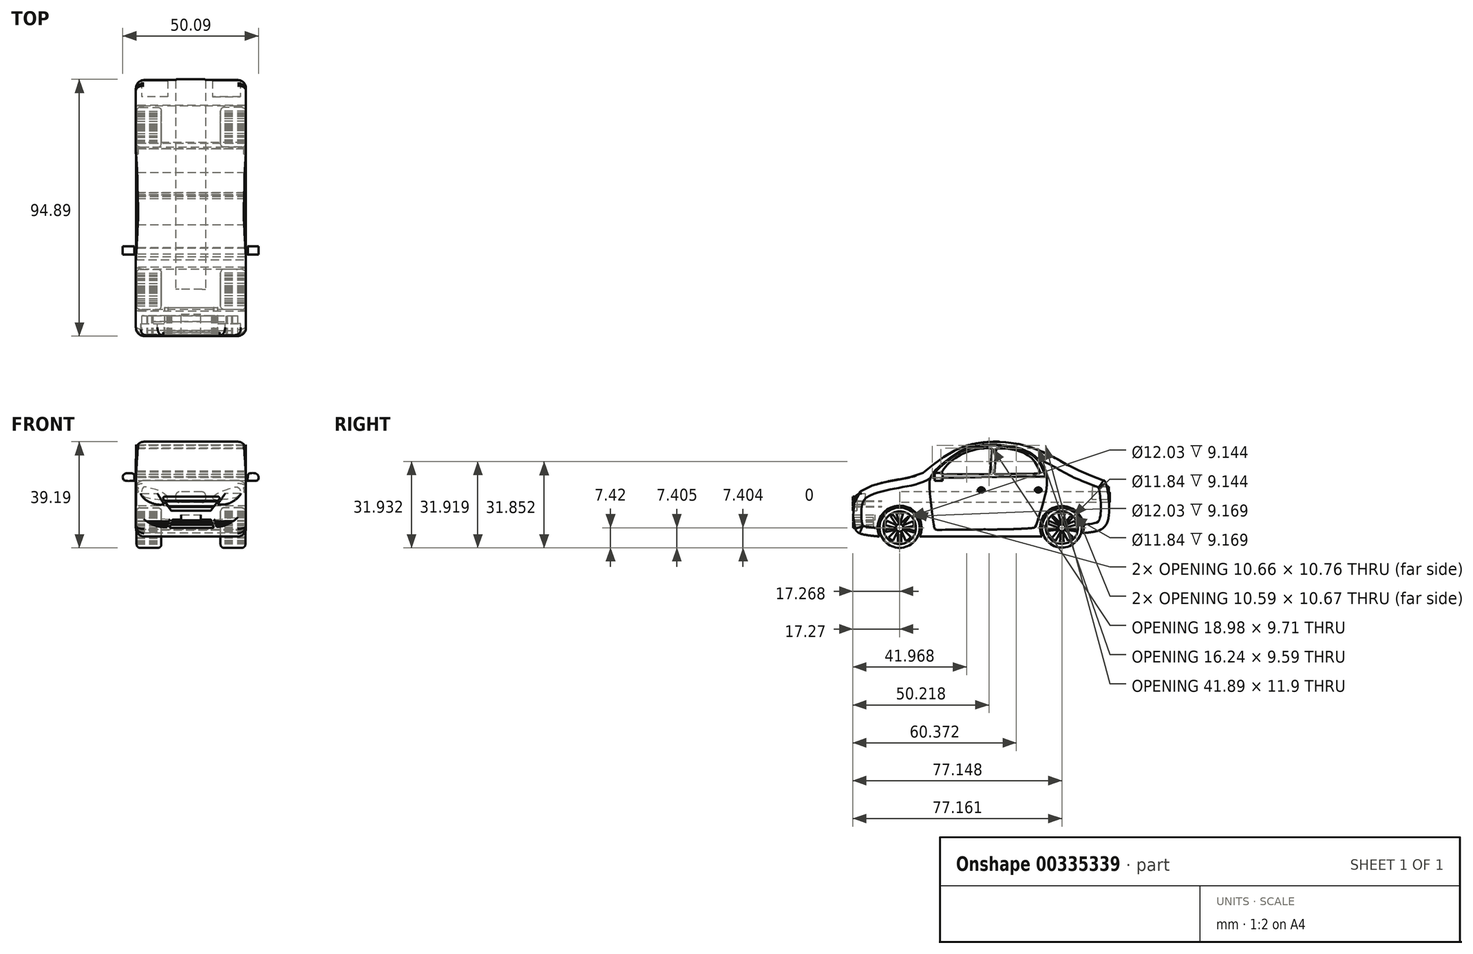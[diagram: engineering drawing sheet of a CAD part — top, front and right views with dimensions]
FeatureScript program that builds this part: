
annotation { "Feature Type Name" : "Feature", "Feature Type Description" : "" }
export const myFeature = defineFeature(function(context is Context, id is Id, definition is map)
    precondition{}
    {
        {
            var Q0;
            Q0=qCreatedBy(makeId("Right.planeOp"),FACE);
            var sketch = newSketch(context, id + "F0", { "sketchPlane" : qUnion([Q0])});
            skCircle(sketch, "E0", {"center": v(0, 0) * mm, "radius": 7.42 * mm});
            skFitSpline(sketch, "E1", {"points": [v(-7.45, -3.27) * mm, v(-16.56, 0) * mm, v(-16.39, 10.61) * mm, v(-12.18, 14.74) * mm, v(-4.1, 17.13) * mm, v(3.13, 18.48) * mm, v(8.44, 20.18) * mm, v(12.58, 23.47) * mm, v(21.8, 29.37) * mm, v(24.6, 30.4) * mm, v(33.03, 31.7) * mm, v(44.35, 30.84) * mm, v(52.91, 27.94) * mm, v(59.85, 24.44) * mm, v(65.24, 21.51) * mm, v(75.37, 17.46) * mm, v(75.38, 17.47) * mm, v(75.88, 16.98) * mm, v(76.75, 2.34) * mm, v(71.8, -1.45) * mm, v(67.68, -1.97) * mm], "startDerivative": vector(-334.75, 36.18) * mm, "endDerivative": vector(-1.84, -0.27) * mm});
            skCircle(sketch, "E2", {"center": v(59.9, -0.02) * mm, "radius": 7.32 * mm});
            skArc(sketch, "E3", {"start": v(7.45, -3.27) * mm, "mid": v(0, 8.13) * mm, "end": v(-7.45, -3.27) * mm});
            skLineSegment(sketch, "E4", {"start": v(7.45, -3.27) * mm, "end": v(52.55, -3.27) * mm});
            skArc(sketch, "E5", {"start": v(67.68, -1.97) * mm, "mid": v(59.2, 7.99) * mm, "end": v(52.55, -3.27) * mm});
            skLineSegment(sketch, "E6", {"start": v(12, 18.48) * mm, "end": v(23.8, 18.48) * mm});
            skLineSegment(sketch, "E7", {"start": v(23.8, 18.48) * mm, "end": v(43.08, 18.82) * mm});
            skFitSpline(sketch, "E8", {"points": [v(43.08, 18.82) * mm, v(53.9, 18.82) * mm], "startDerivative": vector(13.95, 0.43) * mm, "endDerivative": vector(1.45, 0) * mm});
            skFitSpline(sketch, "E9", {"points": [v(12, 18.48) * mm, v(15.51, 22.85) * mm, v(19.98, 26.4) * mm, v(24.84, 28.92) * mm, v(33.06, 30.36) * mm, v(40.04, 29.97) * mm, v(45.26, 28.72) * mm, v(50.5, 25.42) * mm, v(53.9, 18.82) * mm], "startDerivative": vector(25.41, 56.18) * mm, "endDerivative": vector(25.34, -69.35) * mm});
            skLineSegment(sketch, "E10", {"start": v(34.19, 29.32) * mm, "end": v(33.38, 20.5) * mm});
            skLineSegment(sketch, "E11", {"start": v(35.73, 29.3) * mm, "end": v(34.98, 20.88) * mm});
            skFitSpline(sketch, "E12", {"points": [v(33.38, 20.5) * mm, v(33.2, 20.01) * mm, v(32.93, 19.76) * mm, v(32.45, 19.72) * mm, v(30.27, 19.76) * mm, v(15.2, 19.64) * mm], "startDerivative": vector(-1.6, -4.7) * mm, "endDerivative": vector(-36.28, -1.14) * mm});
            skFitSpline(sketch, "E13", {"points": [v(15.2, 19.64) * mm, v(16.6, 22.1) * mm, v(18.32, 23.94) * mm, v(20.98, 26.05) * mm, v(25.02, 27.98) * mm, v(27.97, 28.86) * mm, v(30.54, 29.28) * mm, v(32.47, 29.35) * mm, v(34.19, 29.32) * mm], "startDerivative": vector(6.96, 20.98) * mm, "endDerivative": vector(24.38, -0.14) * mm});
            skFitSpline(sketch, "E14", {"points": [v(34.98, 20.88) * mm, v(35.04, 19.85) * mm, v(35.75, 19.7) * mm, v(43.29, 19.88) * mm, v(51.97, 20.16) * mm, v(51.95, 20.3) * mm, v(50.47, 23.41) * mm, v(47.13, 26.96) * mm, v(43.21, 28.54) * mm, v(39.6, 29.2) * mm, v(35.78, 29.33) * mm, v(35.73, 29.3) * mm], "startDerivative": vector(-4.72, -21.76) * mm, "endDerivative": vector(1.65, -5.9) * mm});
            skFitSpline(sketch, "E15", {"points": [v(34.5, -0.66) * mm, v(31.8, -0.62) * mm, v(27.92, -0.7) * mm, v(15.04, -0.78) * mm, v(13.15, -0.6) * mm, v(12.51, 1.6) * mm, v(11.04, 14.54) * mm, v(11.29, 18.17) * mm, v(12.52, 20.44) * mm, v(13.88, 21.92) * mm, v(16.21, 24.02) * mm, v(17.77, 25.17) * mm, v(19.2, 26.3) * mm, v(21.87, 27.98) * mm, v(23.84, 29.05) * mm, v(26.88, 29.97) * mm, v(30.6, 30.49) * mm, v(33.38, 30.65) * mm, v(35.1, 30.65) * mm, v(38.49, 30.38) * mm, v(42.51, 29.8) * mm, v(44.35, 29.3) * mm, v(46.82, 28.37) * mm, v(49.37, 26.86) * mm, v(51.44, 24.92) * mm, v(53.07, 22.03) * mm, v(53.74, 20.2) * mm, v(54.2, 18.85) * mm, v(54.33, 17.3) * mm, v(54.18, 14.27) * mm, v(52.5, 7.62) * mm, v(50.23, 0.57) * mm, v(49.5, 0) * mm, v(38.73, -0.6) * mm, v(35.9, -0.63) * mm], "startDerivative": vector(-90.1, -4.33) * mm, "endDerivative": vector(-24.37, -0.8) * mm});
            skFitSpline(sketch, "E16", {"points": [v(34.5, -0.66) * mm, v(35.9, -0.63) * mm], "startDerivative": vector(0.82, 0.03) * mm, "endDerivative": vector(0.82, 0.03) * mm});
            skPoint(sketch, "E17.6.internal.snap0", {"position": v(33.78, 24.9) * mm});
            skFitSpline(sketch, "E17", {"points": [v(34.5, -0.66) * mm, v(33.58, 3.26) * mm, v(33.05, 7.57) * mm, v(32.77, 11.15) * mm, v(32.78, 13.96) * mm, v(33.21, 16.71) * mm, v(33.55, 19) * mm, v(34.08, 20.94) * mm, v(34.48, 24.55) * mm, v(34.98, 28.83) * mm, v(35.29, 30.64) * mm], "startDerivative": vector(-4.87, 22.56) * mm, "endDerivative": vector(2.72, 18.18) * mm});
            skFitSpline(sketch, "E18", {"points": [v(9.31, 20.82) * mm, v(10.43, 21.67) * mm, v(11.82, 22.88) * mm, v(13, 23.95) * mm, v(14.9, 25.3) * mm, v(16.2, 26.21) * mm, v(17.35, 26.94) * mm, v(18.48, 27.6) * mm, v(20.2, 28.7) * mm, v(21.78, 29.54) * mm, v(22.77, 29.98) * mm, v(23.55, 30.22) * mm], "startDerivative": vector(16.6, 10.33) * mm, "endDerivative": vector(11.57, 3.51) * mm});
            skArc(sketch, "E19", {"start": v(31.46, 13.96) * mm, "mid": v(30.14, 14.92) * mm, "end": v(28.81, 13.96) * mm});
            skArc(sketch, "E20", {"start": v(28.81, 13.96) * mm, "mid": v(30.14, 13) * mm, "end": v(31.46, 13.96) * mm});
            skLineSegment(sketch, "E21", {"start": v(28.94, 14.24) * mm, "end": v(31.46, 14.28) * mm});
            skLineSegment(sketch, "E22", {"start": v(28.9, 13.74) * mm, "end": v(31.37, 13.74) * mm});
            skLineSegment(sketch, "E23", {"start": v(49.96, 14.17) * mm, "end": v(52.4, 14.17) * mm});
            skLineSegment(sketch, "E24", {"start": v(50, 13.65) * mm, "end": v(52.35, 13.65) * mm});
            skArc(sketch, "E25", {"start": v(52.49, 13.96) * mm, "mid": v(51.18, 14.9) * mm, "end": v(49.87, 13.96) * mm});
            skArc(sketch, "E26", {"start": v(49.87, 13.96) * mm, "mid": v(51.18, 12.98) * mm, "end": v(52.49, 13.96) * mm});
            skCircle(sketch, "E27", {"center": v(0, 0) * mm, "radius": 6.02 * mm});
            skCircle(sketch, "E28", {"center": v(0, 0) * mm, "radius": 5.38 * mm});
            skCircle(sketch, "E29", {"center": v(0, 0) * mm, "radius": 1.37 * mm});
            skLineSegment(sketch, "E30", {"start": v(-1.2, 5.24) * mm, "end": v(-0.05, 1.36) * mm});
            skLineSegment(sketch, "E31", {"start": v(-0.05, 1.36) * mm, "end": v(-2.4, 4.82) * mm});
            skLineSegment(sketch, "E32", {"start": v(0.13, 1.36) * mm, "end": v(1.3, 5.22) * mm});
            skLineSegment(sketch, "E33", {"start": v(0.13, 1.36) * mm, "end": v(3.31, 4.24) * mm});
            skLineSegment(sketch, "E34", {"start": v(-1.06, 0.86) * mm, "end": v(-3.34, 4.22) * mm});
            skLineSegment(sketch, "E35", {"start": v(-1.06, 0.86) * mm, "end": v(-4.72, 2.58) * mm});
            skLineSegment(sketch, "E36", {"start": v(3.6, 4) * mm, "end": v(1.1, 0.81) * mm});
            skLineSegment(sketch, "E37", {"start": v(1.1, 0.81) * mm, "end": v(4.86, 2.3) * mm});
            skLineSegment(sketch, "E38", {"start": v(-1.37, 0) * mm, "end": v(-5.3, 0.97) * mm});
            skLineSegment(sketch, "E39", {"start": v(-1.37, 0) * mm, "end": v(-5.33, -0.7) * mm});
            skLineSegment(sketch, "E40", {"start": v(-1.18, -0.69) * mm, "end": v(-5.15, -1.54) * mm});
            skLineSegment(sketch, "E41", {"start": v(-1.18, -0.69) * mm, "end": v(-4.01, -3.58) * mm});
            skLineSegment(sketch, "E42", {"start": v(1.37, 0) * mm, "end": v(5.33, 0.72) * mm});
            skLineSegment(sketch, "E43", {"start": v(1.37, 0) * mm, "end": v(5.26, -1.1) * mm});
            skLineSegment(sketch, "E44", {"start": v(1.22, -0.61) * mm, "end": v(5.12, -1.65) * mm});
            skLineSegment(sketch, "E45", {"start": v(1.22, -0.61) * mm, "end": v(4.13, -3.45) * mm});
            skLineSegment(sketch, "E46", {"start": v(-2.4, -4.82) * mm, "end": v(-0.6, -1.23) * mm});
            skLineSegment(sketch, "E47", {"start": v(-0.6, -1.23) * mm, "end": v(-0.7, -5.33) * mm});
            skLineSegment(sketch, "E48", {"start": v(0.57, -5.35) * mm, "end": v(0.57, -1.24) * mm});
            skLineSegment(sketch, "E49", {"start": v(0.57, -1.24) * mm, "end": v(2.25, -4.88) * mm});
            skCircle(sketch, "E50", {"center": v(59.9, -0.02) * mm, "radius": 5.92 * mm});
            skCircle(sketch, "E51", {"center": v(59.9, -0.02) * mm, "radius": 5.33 * mm});
            skCircle(sketch, "E52", {"center": v(59.9, -0.02) * mm, "radius": 1.26 * mm});
            skLineSegment(sketch, "E53", {"start": v(60.27, 1.19) * mm, "end": v(60.93, 5.22) * mm});
            skLineSegment(sketch, "E54", {"start": v(60.27, 1.19) * mm, "end": v(63.08, 4.26) * mm});
            skLineSegment(sketch, "E55", {"start": v(58.63, 5.17) * mm, "end": v(59.77, 1.24) * mm});
            skLineSegment(sketch, "E56", {"start": v(59.77, 1.24) * mm, "end": v(56.79, 4.32) * mm});
            skLineSegment(sketch, "E57", {"start": v(56.27, 3.9) * mm, "end": v(59, 0.88) * mm});
            skLineSegment(sketch, "E58", {"start": v(59, 0.88) * mm, "end": v(55.18, 2.48) * mm});
            skLineSegment(sketch, "E59", {"start": v(60.8, 0.87) * mm, "end": v(63.77, 3.65) * mm});
            skLineSegment(sketch, "E60", {"start": v(60.8, 0.87) * mm, "end": v(64.6, 2.47) * mm});
            skLineSegment(sketch, "E61", {"start": v(60.6, -5.3) * mm, "end": v(60.17, -1.25) * mm});
            skPoint(sketch, "E61.startSnap0", {"position": v(60.6, 3.2) * mm});
            skLineSegment(sketch, "E62", {"start": v(60.17, -1.25) * mm, "end": v(62.16, -4.84) * mm});
            skLineSegment(sketch, "E63", {"start": v(59.15, -5.3) * mm, "end": v(59.59, -1.24) * mm});
            skLineSegment(sketch, "E64", {"start": v(59.59, -1.24) * mm, "end": v(57.58, -4.82) * mm});
            skLineSegment(sketch, "E65", {"start": v(61.15, 0.1) * mm, "end": v(65.1, 1.12) * mm});
            skLineSegment(sketch, "E66", {"start": v(61.15, 0.1) * mm, "end": v(65.18, -0.73) * mm});
            skLineSegment(sketch, "E67", {"start": v(65.05, -1.38) * mm, "end": v(60.97, -0.67) * mm});
            skLineSegment(sketch, "E68", {"start": v(60.97, -0.67) * mm, "end": v(64, -3.43) * mm});
            skLineSegment(sketch, "E69", {"start": v(58.63, 0) * mm, "end": v(54.77, 1.47) * mm});
            skLineSegment(sketch, "E70", {"start": v(58.63, 0) * mm, "end": v(54.58, -0.51) * mm});
            skLineSegment(sketch, "E71", {"start": v(54.69, -1.18) * mm, "end": v(58.84, -0.72) * mm});
            skLineSegment(sketch, "E72", {"start": v(58.84, -0.72) * mm, "end": v(56.16, -3.82) * mm});
            skFitSpline(sketch, "E73", {"points": [v(67.76, -1.96) * mm, v(67.68, -1.97) * mm], "startDerivative": vector(-0.1, 0) * mm, "endDerivative": vector(-0.05, 0) * mm});
            skFitSpline(sketch, "E74", {"points": [v(63.64, 22.4) * mm, v(59.31, 24.8) * mm, v(56.3, 26.43) * mm, v(54.3, 27.37) * mm, v(50.96, 28.83) * mm, v(49.58, 29.37) * mm, v(48.2, 29.85) * mm], "startDerivative": vector(-23.68, 12.38) * mm, "endDerivative": vector(-10.9, 3.6) * mm});
            skFitSpline(sketch, "E75", {"points": [v(67.77, -1.99) * mm, v(68.13, -1.96) * mm, v(68.42, -1.93) * mm, v(69.26, -1.86) * mm, v(70.44, -1.71) * mm, v(70.82, -1.66) * mm, v(71.21, -1.6) * mm, v(71.94, -1.48) * mm, v(73.05, -1.24) * mm, v(73.32, -1.18) * mm, v(73.58, -1.08) * mm, v(73.78, -1) * mm, v(73.96, -0.9) * mm, v(74.23, -0.8) * mm, v(74.42, -0.7) * mm, v(74.66, -0.57) * mm, v(74.78, -0.48) * mm, v(74.94, -0.39) * mm, v(75.25, -0.11) * mm, v(75.42, 0.03) * mm, v(75.56, 0.15) * mm, v(75.69, 0.29) * mm, v(75.82, 0.44) * mm, v(75.92, 0.6) * mm, v(75.96, 0.64) * mm, v(76, 0.7) * mm, v(76.01, 0.73) * mm, v(76.07, 0.82) * mm, v(76.14, 0.92) * mm, v(76.23, 1.07) * mm, v(76.33, 1.26) * mm, v(76.46, 1.51) * mm, v(76.47, 1.55) * mm, v(76.49, 1.6) * mm, v(76.5, 1.65) * mm], "startDerivative": vector(11.27, 0.92) * mm, "endDerivative": vector(3.7, 8.89) * mm});
            skSolve(sketch);
        }
        {
            var Q0;
            Q0=makeQuery(id+"F0.imprint","IMPRINT",FACE,{"disambiguationData":[TD([[makeQuery(id+"F0.imprint","IMPRINT",EDGE,{"derivedFrom":sQuery(id+"F0.wireOp",EDGE,"E1")}),-1.0]])]});
            extrude(context, id + "F1", {"entities" : qUnion([Q0]), "depth" : 20.32 * mm, "hasSecondDirection" : true, "secondDirectionOppositeDirection" : true, "secondDirectionDepth" : 20.32 * mm});
        }
        {
            var Q0;
            Q0=makeQuery(id+"F0.imprint","IMPRINT",FACE,{"disambiguationData":[TD([[makeQuery(id+"F0.imprint","IMPRINT",EDGE,{"derivedFrom":sQuery(id+"F0.wireOp",EDGE,"E10")}),-1.0]])]});
            var Q1;
            Q1=makeQuery(id+"F0.imprint","IMPRINT",FACE,{"disambiguationData":[TD([[makeQuery(id+"F0.imprint","IMPRINT",EDGE,{"derivedFrom":sQuery(id+"F0.wireOp",EDGE,"E11")}),1.0]])]});
            extrude(context, id + "F2", {"entities" : qUnion([Q0, Q1]), "depth" : 20.07 * mm, "hasSecondDirection" : true, "secondDirectionOppositeDirection" : true, "secondDirectionDepth" : 20.07 * mm});
        }
        {
            var Q0;
            {var subQ1=sQuery(id+"F0.wireOp",EDGE,"E6");Q0=makeQuery(id+"F0.imprint","IMPRINT",FACE,{"disambiguationData":[TD([[makeQuery(id+"F0.imprint","IMPRINT",EDGE,{"derivedFrom":subQ1}),1.0]])]});}
            var Q1;
            {var subQ1=sQuery(id+"F0.wireOp",EDGE,"E8");Q1=makeQuery(id+"F0.imprint","IMPRINT",FACE,{"disambiguationData":[TD([[makeQuery(id+"F0.imprint","IMPRINT",EDGE,{"derivedFrom":subQ1}),1.0]])]});}
            extrude(context, id + "F3", {"entities" : qUnion([Q0, Q1]), "depth" : 20.14 * mm, "hasSecondDirection" : true, "secondDirectionOppositeDirection" : true, "secondDirectionDepth" : 20.14 * mm});
        }
        {
            var Q0;
            {var subQ1=sQuery(id+"F0.wireOp",EDGE,"E8");Q0=makeQuery(id+"F0.imprint","IMPRINT",FACE,{"disambiguationData":[TD([[makeQuery(id+"F0.imprint","IMPRINT",EDGE,{"derivedFrom":subQ1}),-1.0]])]});}
            var Q1;
            {var subQ1=sQuery(id+"F0.wireOp",EDGE,"E6");Q1=makeQuery(id+"F0.imprint","IMPRINT",FACE,{"disambiguationData":[TD([[makeQuery(id+"F0.imprint","IMPRINT",EDGE,{"derivedFrom":subQ1}),-1.0]])]});}
            extrude(context, id + "F4", {"entities" : qUnion([Q0, Q1]), "depth" : 20.24 * mm, "hasSecondDirection" : true, "secondDirectionOppositeDirection" : true, "secondDirectionDepth" : 20.24 * mm});
        }
        {
            var Q0;
            Q0=sQuery(id+"F0.wireOp",EDGE,"E17");
            extrude(context, id + "F5", {"bodyType" : ToolBodyType.SURFACE, "surfaceEntities" : qUnion([Q0]), "depth" : 20.17 * mm, "hasSecondDirection" : true, "secondDirectionOppositeDirection" : true, "secondDirectionDepth" : 20.17 * mm});
        }
        {
            var Q0;
            Q0=qCreatedBy(makeId("Front.planeOp"),FACE);
            var sketch = newSketch(context, id + "F6", { "sketchPlane" : qUnion([Q0])});
            skLineSegment(sketch, "E76", {"start": v(18.39, 12.66) * mm, "end": v(12.65, 12.66) * mm});
            skLineSegment(sketch, "E77", {"start": v(12.65, 12.66) * mm, "end": v(9.9, 8.59) * mm});
            skFitSpline(sketch, "E78", {"points": [v(9.9, 8.59) * mm, v(13.32, 8.77) * mm, v(15.04, 9.46) * mm, v(16.44, 10.37) * mm, v(18.39, 12.66) * mm], "startDerivative": vector(11.8, -1.45) * mm, "endDerivative": vector(2.65, 9.5) * mm});
            skLineSegment(sketch, "E79", {"start": v(-18.43, 12.66) * mm, "end": v(-12.37, 12.66) * mm});
            skPoint(sketch, "E79.startSnap0", {"position": v(15.52, 12.66) * mm});
            skLineSegment(sketch, "E80", {"start": v(-12.37, 12.66) * mm, "end": v(-9.87, 8.59) * mm});
            skFitSpline(sketch, "E81", {"points": [v(-18.43, 12.66) * mm, v(-17.56, 11.07) * mm, v(-16.28, 10.01) * mm, v(-14.96, 9.33) * mm, v(-13.42, 8.77) * mm, v(-12.15, 8.55) * mm, v(-9.87, 8.59) * mm], "startDerivative": vector(-1.23, -8.9) * mm, "endDerivative": vector(19.02, 1.78) * mm});
            skLineSegment(sketch, "E82", {"start": v(-9.74, 11.45) * mm, "end": v(10.07, 11.45) * mm});
            skLineSegment(sketch, "E83", {"start": v(10.48, 10.64) * mm, "end": v(7.42, 6.46) * mm});
            skLineSegment(sketch, "E84", {"start": v(7, 6.25) * mm, "end": v(-7.04, 6.25) * mm});
            skLineSegment(sketch, "E85", {"start": v(-7.47, 6.49) * mm, "end": v(-10.16, 10.66) * mm});
            skPoint(sketch, "E86.visualSharp", {"position": v(-10.67, 11.45) * mm});
            skArc(sketch, "E86.filletArc", {"start": v(-9.74, 11.45) * mm, "mid": v(-10.18, 11.18) * mm, "end": v(-10.16, 10.66) * mm});
            skPoint(sketch, "E87.visualSharp", {"position": v(11.07, 11.45) * mm});
            skArc(sketch, "E87.filletArc", {"start": v(10.48, 10.64) * mm, "mid": v(10.52, 11.17) * mm, "end": v(10.07, 11.45) * mm});
            skPoint(sketch, "E88.visualSharp", {"position": v(7.27, 6.25) * mm});
            skArc(sketch, "E88.filletArc", {"start": v(7, 6.25) * mm, "mid": v(7.24, 6.3) * mm, "end": v(7.42, 6.46) * mm});
            skPoint(sketch, "E89.visualSharp", {"position": v(-7.32, 6.25) * mm});
            skArc(sketch, "E89.filletArc", {"start": v(-7.47, 6.49) * mm, "mid": v(-7.29, 6.32) * mm, "end": v(-7.04, 6.25) * mm});
            skLineSegment(sketch, "E90", {"start": v(-9.74, 10) * mm, "end": v(10.01, 10) * mm});
            skLineSegment(sketch, "E91", {"start": v(-9.57, 9.74) * mm, "end": v(9.82, 9.74) * mm});
            skLineSegment(sketch, "E92", {"start": v(-8.45, 8) * mm, "end": v(8.55, 8) * mm});
            skLineSegment(sketch, "E93", {"start": v(-8.27, 7.73) * mm, "end": v(8.35, 7.73) * mm});
            skLineSegment(sketch, "E94", {"start": v(-6.7, 3) * mm, "end": v(7.3, 3) * mm});
            skLineSegment(sketch, "E95", {"start": v(7.5, 2.86) * mm, "end": v(8.38, 0.27) * mm});
            skLineSegment(sketch, "E96", {"start": v(8.19, 0) * mm, "end": v(-7.6, 0) * mm});
            skLineSegment(sketch, "E97", {"start": v(-7.8, 0.27) * mm, "end": v(-6.88, 2.86) * mm});
            skLineSegment(sketch, "E98", {"start": v(8.63, 2.68) * mm, "end": v(9.45, 0.26) * mm});
            skLineSegment(sketch, "E99", {"start": v(8.8, 2.95) * mm, "end": v(17.3, 3.88) * mm});
            skArc(sketch, "E100", {"start": v(9.45, 0.26) * mm, "mid": v(13.72, 1.34) * mm, "end": v(17.3, 3.88) * mm});
            skLineSegment(sketch, "E101", {"start": v(-7.84, 2.67) * mm, "end": v(-8.77, 0.21) * mm});
            skLineSegment(sketch, "E102", {"start": v(-8, 2.95) * mm, "end": v(-18.1, 3.88) * mm});
            skArc(sketch, "E103", {"start": v(-18.1, 3.88) * mm, "mid": v(-13.84, 1.03) * mm, "end": v(-8.77, 0.21) * mm});
            skLineSegment(sketch, "E104", {"start": v(-7.08, 2.3) * mm, "end": v(7.69, 2.3) * mm});
            skLineSegment(sketch, "E105", {"start": v(7.69, 2.3) * mm, "end": v(7.76, 2.09) * mm});
            skLineSegment(sketch, "E106", {"start": v(7.76, 2.09) * mm, "end": v(-7.16, 2.09) * mm});
            skLineSegment(sketch, "E107", {"start": v(8.04, 1.26) * mm, "end": v(-7.45, 1.26) * mm});
            skLineSegment(sketch, "E108", {"start": v(-7.45, 1.26) * mm, "end": v(-7.52, 1.04) * mm});
            skLineSegment(sketch, "E109", {"start": v(-7.52, 1.04) * mm, "end": v(8.12, 1.04) * mm});
            skLineSegment(sketch, "E110", {"start": v(-7.97, 2.3) * mm, "end": v(-16.24, 2.3) * mm});
            skLineSegment(sketch, "E111", {"start": v(-8.06, 2.09) * mm, "end": v(-15.91, 2.09) * mm});
            skLineSegment(sketch, "E112", {"start": v(-8.37, 1.26) * mm, "end": v(-14.38, 1.26) * mm});
            skLineSegment(sketch, "E113", {"start": v(-8.46, 1.04) * mm, "end": v(-13.85, 1.04) * mm});
            skLineSegment(sketch, "E114", {"start": v(8.75, 2.3) * mm, "end": v(15.43, 2.3) * mm});
            skLineSegment(sketch, "E115", {"start": v(8.83, 2.09) * mm, "end": v(15.1, 2.09) * mm});
            skLineSegment(sketch, "E116", {"start": v(9.11, 1.26) * mm, "end": v(13.53, 1.26) * mm});
            skLineSegment(sketch, "E117", {"start": v(9.19, 1.04) * mm, "end": v(13, 1.04) * mm});
            skLineSegment(sketch, "E118", {"start": v(-3.6, 4.76) * mm, "end": v(3.6, 4.76) * mm});
            skLineSegment(sketch, "E119", {"start": v(3.6, 4.76) * mm, "end": v(3.6, 2.7) * mm});
            skLineSegment(sketch, "E120", {"start": v(3.6, 2.7) * mm, "end": v(-3.6, 2.7) * mm});
            skLineSegment(sketch, "E121", {"start": v(-3.6, 2.7) * mm, "end": v(-3.6, 4.76) * mm});
            skPoint(sketch, "E122.visualSharp", {"position": v(7.45, 3) * mm});
            skArc(sketch, "E122.filletArc", {"start": v(7.5, 2.86) * mm, "mid": v(7.42, 2.96) * mm, "end": v(7.3, 3) * mm});
            skPoint(sketch, "E123.visualSharp", {"position": v(8.47, 0) * mm});
            skArc(sketch, "E123.filletArc", {"start": v(8.19, 0) * mm, "mid": v(8.35, 0.08) * mm, "end": v(8.38, 0.27) * mm});
            skPoint(sketch, "E124.visualSharp", {"position": v(-6.84, 3) * mm});
            skArc(sketch, "E124.filletArc", {"start": v(-6.7, 3) * mm, "mid": v(-6.8, 2.96) * mm, "end": v(-6.88, 2.86) * mm});
            skPoint(sketch, "E125.visualSharp", {"position": v(-7.89, 0) * mm});
            skArc(sketch, "E125.filletArc", {"start": v(-7.8, 0.27) * mm, "mid": v(-7.77, 0.09) * mm, "end": v(-7.6, 0) * mm});
            skPoint(sketch, "E126.visualSharp", {"position": v(-7.74, 2.92) * mm});
            skArc(sketch, "E126.filletArc", {"start": v(-7.84, 2.67) * mm, "mid": v(-7.85, 2.85) * mm, "end": v(-8, 2.95) * mm});
            skPoint(sketch, "E127.visualSharp", {"position": v(8.54, 2.92) * mm});
            skArc(sketch, "E127.filletArc", {"start": v(8.8, 2.95) * mm, "mid": v(8.65, 2.86) * mm, "end": v(8.63, 2.68) * mm});
            skSolve(sketch);
        }
        {
            var Q0;
            Q0=makeQuery(id+"F6.imprint","IMPRINT",FACE,{"disambiguationData":[TD([[makeQuery(id+"F6.imprint","IMPRINT",EDGE,{"derivedFrom":sQuery(id+"F6.wireOp",EDGE,"E79")}),-1.0]])]});
            var Q1;
            Q1=makeQuery(id+"F6.imprint","IMPRINT",FACE,{"disambiguationData":[TD([[makeQuery(id+"F6.imprint","IMPRINT",EDGE,{"derivedFrom":sQuery(id+"F6.wireOp",EDGE,"E76")}),1.0]])]});
            extrude(context, id + "F7", {"entities" : qUnion([Q0, Q1]), "depth" : 16.97 * mm, "hasSecondDirection" : true, "secondDirectionOppositeDirection" : false, "secondDirectionDepth" : 12.7 * mm});
        }
        {
            var Q0;
            Q0=makeQuery(id+"F1.opExtrude","CAP_EDGE",EDGE,{"disambiguationData":[OSD([sQuery(id+"F0.wireOp",EDGE,"E4")])],"isStart":false});
            var Q1;
            Q1=makeQuery(id+"F1.opExtrude","CAP_EDGE",EDGE,{"disambiguationData":[OSD([sQuery(id+"F0.wireOp",EDGE,"E4")])],"isStart":true});
            fillet(context, id + "F8", {"entities" : qUnion([Q0, Q1]), "radius" : 3.56 * mm, "tangentPropagation" : true, "allowEdgeOverflow" : false});
        }
        {
            var Q0;
            Q0=sQuery(id+"F0.wireOp",EDGE,"E18");
            extrude(context, id + "F9", {"bodyType" : ToolBodyType.SURFACE, "surfaceEntities" : qUnion([Q0]), "depth" : 17.02 * mm, "hasSecondDirection" : true, "secondDirectionOppositeDirection" : true, "secondDirectionDepth" : 17.02 * mm});
        }
        {
            var Q0;
            {var subQ0=sQuery(id+"F0.wireOp",EDGE,"E1");Q0=makeQuery(id+"F1.opExtrude","CAP_EDGE",EDGE,{"disambiguationData":[OSD([subQ0]),TDD([makeQuery(id+"F0.imprint","IMPRINT",EDGE,{"disambiguationData":[TD([[makeQuery(id+"F0.imprint","INTERSECT",VERTEX,{"derivedFrom":[subQ0,sQuery(id+"F0.wireOp",EDGE,"E3")]}),-1.0]])],"derivedFrom":subQ0})])],"isStart":true});}
            var Q1;
            {var subQ0=sQuery(id+"F0.wireOp",EDGE,"E1");Q1=makeQuery(id+"F1.opExtrude","CAP_EDGE",EDGE,{"disambiguationData":[OSD([subQ0]),TDD([makeQuery(id+"F0.imprint","IMPRINT",EDGE,{"disambiguationData":[TD([[makeQuery(id+"F0.imprint","INTERSECT",VERTEX,{"derivedFrom":[subQ0,sQuery(id+"F0.wireOp",EDGE,"E3")]}),-1.0]])],"derivedFrom":subQ0})])],"isStart":false});}
            var Q2;
            {var subQ0=sQuery(id+"F0.wireOp",EDGE,"E1");Q2=makeQuery(id+"F1.opExtrude","CAP_EDGE",EDGE,{"disambiguationData":[OSD([subQ0]),TDD([makeQuery(id+"F0.imprint","IMPRINT",EDGE,{"disambiguationData":[TD([[makeQuery(id+"F0.imprint","INTERSECT",VERTEX,{"derivedFrom":[subQ0,sQuery(id+"F0.wireOp",EDGE,"E73")]}),1.0]])],"derivedFrom":subQ0})])],"isStart":false});}
            var Q3;
            {var subQ0=sQuery(id+"F0.wireOp",EDGE,"E1");Q3=makeQuery(id+"F1.opExtrude","CAP_EDGE",EDGE,{"disambiguationData":[OSD([subQ0]),TDD([makeQuery(id+"F0.imprint","IMPRINT",EDGE,{"disambiguationData":[TD([[makeQuery(id+"F0.imprint","INTERSECT",VERTEX,{"derivedFrom":[subQ0,sQuery(id+"F0.wireOp",EDGE,"E73")]}),1.0]])],"derivedFrom":subQ0})])],"isStart":true});}
            fillet(context, id + "F10", {"entities" : qUnion([Q0, Q1, Q2, Q3]), "radius" : 3.05 * mm, "tangentPropagation" : true, "allowEdgeOverflow" : false});
        }
        {
            var Q0;
            Q0=makeQuery(id+"F7.opExtrude","CAP_EDGE",EDGE,{"disambiguationData":[OSD([sQuery(id+"F6.wireOp",EDGE,"E79")])],"isStart":false});
            var Q1;
            Q1=makeQuery(id+"F7.opExtrude","CAP_EDGE",EDGE,{"disambiguationData":[OSD([sQuery(id+"F6.wireOp",EDGE,"E76")])],"isStart":false});
            fillet(context, id + "F11", {"entities" : qUnion([Q0, Q1]), "radius" : 2.94 * mm, "tangentPropagation" : true, "allowEdgeOverflow" : false});
        }
        {
            var Q0;
            {var subQ0=sQuery(id+"F0.wireOp",EDGE,"E21");var subQ1=sQuery(id+"F0.wireOp",EDGE,"E19");var subQ2=makeQuery(id+"F0.imprint","INTERSECT",VERTEX,{"disambiguationData":[OD(0.0)],"derivedFrom":[subQ1,subQ0]});Q0=makeQuery(id+"F0.imprint","IMPRINT",FACE,{"disambiguationData":[TD([[makeQuery(id+"F0.imprint","IMPRINT",EDGE,{"disambiguationData":[TD([[subQ2,1.0]])],"derivedFrom":subQ1}),1.0]])]});}
            var Q1;
            {var subQ0=sQuery(id+"F0.wireOp",EDGE,"E22");Q1=makeQuery(id+"F0.imprint","IMPRINT",FACE,{"disambiguationData":[TD([[makeQuery(id+"F0.imprint","IMPRINT",EDGE,{"derivedFrom":subQ0}),-1.0]])]});}
            var Q2;
            {var subQ0=sQuery(id+"F0.wireOp",EDGE,"E24");Q2=makeQuery(id+"F0.imprint","IMPRINT",FACE,{"disambiguationData":[TD([[makeQuery(id+"F0.imprint","IMPRINT",EDGE,{"derivedFrom":subQ0}),-1.0]])]});}
            var Q3;
            {var subQ0=sQuery(id+"F0.wireOp",EDGE,"E23");Q3=makeQuery(id+"F0.imprint","IMPRINT",FACE,{"disambiguationData":[TD([[makeQuery(id+"F0.imprint","IMPRINT",EDGE,{"derivedFrom":subQ0}),1.0]])]});}
            extrude(context, id + "F12", {"entities" : qUnion([Q0, Q1, Q2, Q3]), "operationType" : NewBodyOperationType.ADD, "depth" : 19.53 * mm, "hasSecondDirection" : true, "secondDirectionOppositeDirection" : true, "secondDirectionDepth" : 19.53 * mm});
        }
        {
            var Q0;
            {var subQ3=sQuery(id+"F0.wireOp",EDGE,"E22");Q0=makeQuery(id+"F0.imprint","IMPRINT",FACE,{"disambiguationData":[TD([[makeQuery(id+"F0.imprint","IMPRINT",EDGE,{"derivedFrom":subQ3}),1.0]])]});}
            var Q1;
            {var subQ1=sQuery(id+"F0.wireOp",EDGE,"E23");Q1=makeQuery(id+"F0.imprint","IMPRINT",FACE,{"disambiguationData":[TD([[makeQuery(id+"F0.imprint","IMPRINT",EDGE,{"derivedFrom":subQ1}),-1.0]])]});}
            extrude(context, id + "F13", {"entities" : qUnion([Q0, Q1]), "operationType" : NewBodyOperationType.ADD, "depth" : 20.26 * mm, "hasSecondDirection" : true, "secondDirectionOppositeDirection" : true, "secondDirectionDepth" : 20.27 * mm});
        }
        {
            var Q0;
            {var subQ0=sQuery(id+"F6.wireOp",EDGE,"E92");Q0=makeQuery(id+"F6.imprint","IMPRINT",FACE,{"disambiguationData":[TD([[makeQuery(id+"F6.imprint","IMPRINT",EDGE,{"derivedFrom":subQ0}),-1.0]])]});}
            var Q1;
            {var subQ0=sQuery(id+"F6.wireOp",EDGE,"E90");Q1=makeQuery(id+"F6.imprint","IMPRINT",FACE,{"disambiguationData":[TD([[makeQuery(id+"F6.imprint","IMPRINT",EDGE,{"derivedFrom":subQ0}),-1.0]])]});}
            extrude(context, id + "F14", {"entities" : qUnion([Q0, Q1]), "depth" : 17.04 * mm, "hasSecondDirection" : true, "secondDirectionOppositeDirection" : false, "secondDirectionDepth" : 6.63 * mm});
        }
        {
            var Q0;
            Q0=makeQuery(id+"F6.imprint","IMPRINT",FACE,{"disambiguationData":[TD([[makeQuery(id+"F6.imprint","IMPRINT",EDGE,{"derivedFrom":sQuery(id+"F6.wireOp",EDGE,"E84")}),-1.0]])]});
            var Q1;
            Q1=makeQuery(id+"F6.imprint","IMPRINT",FACE,{"disambiguationData":[TD([[makeQuery(id+"F6.imprint","IMPRINT",EDGE,{"derivedFrom":sQuery(id+"F6.wireOp",EDGE,"E82")}),-1.0]])]});
            var Q2;
            {var subQ0=sQuery(id+"F6.wireOp",EDGE,"E91");Q2=makeQuery(id+"F6.imprint","IMPRINT",FACE,{"disambiguationData":[TD([[makeQuery(id+"F6.imprint","IMPRINT",EDGE,{"derivedFrom":subQ0}),-1.0]])]});}
            extrude(context, id + "F15", {"entities" : qUnion([Q0, Q1, Q2]), "depth" : 17.27 * mm, "hasSecondDirection" : true, "secondDirectionOppositeDirection" : false, "secondDirectionDepth" : 15.8 * mm});
        }
        {
            var Q0;
            Q0=makeQuery(id+"F0.imprint","IMPRINT",FACE,{"disambiguationData":[TD([[makeQuery(id+"F0.imprint","IMPRINT",EDGE,{"derivedFrom":sQuery(id+"F0.wireOp",EDGE,"E0")}),1.0]])]});
            var Q1;
            {var subQ0=sQuery(id+"F0.wireOp",EDGE,"E30");Q1=makeQuery(id+"F0.imprint","IMPRINT",FACE,{"disambiguationData":[TD([[makeQuery(id+"F0.imprint","IMPRINT",EDGE,{"derivedFrom":subQ0}),1.0]])]});}
            var Q2;
            {var subQ0=sQuery(id+"F0.wireOp",EDGE,"E31");Q2=makeQuery(id+"F0.imprint","IMPRINT",FACE,{"disambiguationData":[TD([[makeQuery(id+"F0.imprint","IMPRINT",EDGE,{"derivedFrom":subQ0}),1.0]])]});}
            var Q3;
            {var subQ0=sQuery(id+"F0.wireOp",EDGE,"E33");Q3=makeQuery(id+"F0.imprint","IMPRINT",FACE,{"disambiguationData":[TD([[makeQuery(id+"F0.imprint","IMPRINT",EDGE,{"derivedFrom":subQ0}),-1.0]])]});}
            var Q4;
            {var subQ0=sQuery(id+"F0.wireOp",EDGE,"E39");Q4=makeQuery(id+"F0.imprint","IMPRINT",FACE,{"disambiguationData":[TD([[makeQuery(id+"F0.imprint","IMPRINT",EDGE,{"derivedFrom":subQ0}),1.0]])]});}
            var Q5;
            {var subQ0=sQuery(id+"F0.wireOp",EDGE,"E43");Q5=makeQuery(id+"F0.imprint","IMPRINT",FACE,{"disambiguationData":[TD([[makeQuery(id+"F0.imprint","IMPRINT",EDGE,{"derivedFrom":subQ0}),-1.0]])]});}
            var Q6;
            {var subQ0=sQuery(id+"F0.wireOp",EDGE,"E35");Q6=makeQuery(id+"F0.imprint","IMPRINT",FACE,{"disambiguationData":[TD([[makeQuery(id+"F0.imprint","IMPRINT",EDGE,{"derivedFrom":subQ0}),1.0]])]});}
            var Q7;
            {var subQ0=sQuery(id+"F0.wireOp",EDGE,"E37");Q7=makeQuery(id+"F0.imprint","IMPRINT",FACE,{"disambiguationData":[TD([[makeQuery(id+"F0.imprint","IMPRINT",EDGE,{"derivedFrom":subQ0}),-1.0]])]});}
            var Q8;
            {var subQ0=sQuery(id+"F0.wireOp",EDGE,"E41");Q8=makeQuery(id+"F0.imprint","IMPRINT",FACE,{"disambiguationData":[TD([[makeQuery(id+"F0.imprint","IMPRINT",EDGE,{"derivedFrom":subQ0}),1.0]])]});}
            var Q9;
            {var subQ0=sQuery(id+"F0.wireOp",EDGE,"E45");Q9=makeQuery(id+"F0.imprint","IMPRINT",FACE,{"disambiguationData":[TD([[makeQuery(id+"F0.imprint","IMPRINT",EDGE,{"derivedFrom":subQ0}),-1.0]])]});}
            var Q10;
            {var subQ0=sQuery(id+"F0.wireOp",EDGE,"E47");Q10=makeQuery(id+"F0.imprint","IMPRINT",FACE,{"disambiguationData":[TD([[makeQuery(id+"F0.imprint","IMPRINT",EDGE,{"derivedFrom":subQ0}),1.0]])]});}
            var Q11;
            Q11=makeQuery(id+"F0.imprint","IMPRINT",FACE,{"disambiguationData":[TD([[makeQuery(id+"F0.imprint","IMPRINT",EDGE,{"derivedFrom":sQuery(id+"F0.wireOp",EDGE,"E2")}),1.0]])]});
            var Q12;
            {var subQ0=sQuery(id+"F0.wireOp",EDGE,"E53");Q12=makeQuery(id+"F0.imprint","IMPRINT",FACE,{"disambiguationData":[TD([[makeQuery(id+"F0.imprint","IMPRINT",EDGE,{"derivedFrom":subQ0}),1.0]])]});}
            var Q13;
            {var subQ0=sQuery(id+"F0.wireOp",EDGE,"E56");Q13=makeQuery(id+"F0.imprint","IMPRINT",FACE,{"disambiguationData":[TD([[makeQuery(id+"F0.imprint","IMPRINT",EDGE,{"derivedFrom":subQ0}),1.0]])]});}
            var Q14;
            {var subQ0=sQuery(id+"F0.wireOp",EDGE,"E58");Q14=makeQuery(id+"F0.imprint","IMPRINT",FACE,{"disambiguationData":[TD([[makeQuery(id+"F0.imprint","IMPRINT",EDGE,{"derivedFrom":subQ0}),1.0]])]});}
            var Q15;
            {var subQ0=sQuery(id+"F0.wireOp",EDGE,"E70");Q15=makeQuery(id+"F0.imprint","IMPRINT",FACE,{"disambiguationData":[TD([[makeQuery(id+"F0.imprint","IMPRINT",EDGE,{"derivedFrom":subQ0}),1.0]])]});}
            var Q16;
            {var subQ0=sQuery(id+"F0.wireOp",EDGE,"E66");Q16=makeQuery(id+"F0.imprint","IMPRINT",FACE,{"disambiguationData":[TD([[makeQuery(id+"F0.imprint","IMPRINT",EDGE,{"derivedFrom":subQ0}),-1.0]])]});}
            var Q17;
            {var subQ0=sQuery(id+"F0.wireOp",EDGE,"E54");Q17=makeQuery(id+"F0.imprint","IMPRINT",FACE,{"disambiguationData":[TD([[makeQuery(id+"F0.imprint","IMPRINT",EDGE,{"derivedFrom":subQ0}),-1.0]])]});}
            var Q18;
            {var subQ0=sQuery(id+"F0.wireOp",EDGE,"E62");Q18=makeQuery(id+"F0.imprint","IMPRINT",FACE,{"disambiguationData":[TD([[makeQuery(id+"F0.imprint","IMPRINT",EDGE,{"derivedFrom":subQ0}),1.0]])]});}
            var Q19;
            {var subQ0=sQuery(id+"F0.wireOp",EDGE,"E64");Q19=makeQuery(id+"F0.imprint","IMPRINT",FACE,{"disambiguationData":[TD([[makeQuery(id+"F0.imprint","IMPRINT",EDGE,{"derivedFrom":subQ0}),-1.0]])]});}
            var Q20;
            {var subQ0=sQuery(id+"F0.wireOp",EDGE,"E61");Q20=makeQuery(id+"F0.imprint","IMPRINT",FACE,{"disambiguationData":[TD([[makeQuery(id+"F0.imprint","IMPRINT",EDGE,{"derivedFrom":subQ0}),1.0]])]});}
            var Q21;
            {var subQ0=sQuery(id+"F0.wireOp",EDGE,"E60");Q21=makeQuery(id+"F0.imprint","IMPRINT",FACE,{"disambiguationData":[TD([[makeQuery(id+"F0.imprint","IMPRINT",EDGE,{"derivedFrom":subQ0}),-1.0]])]});}
            extrude(context, id + "F16", {"entities" : qUnion([Q0, Q1, Q2, Q3, Q4, Q5, Q6, Q7, Q8, Q9, Q10, Q11, Q12, Q13, Q14, Q15, Q16, Q17, Q18, Q19, Q20, Q21]), "depth" : 20.1 * mm, "hasSecondDirection" : true, "secondDirectionOppositeDirection" : false, "secondDirectionDepth" : 10.92 * mm});
        }
        {
            var Q0;
            Q0=makeQuery(id+"F0.imprint","IMPRINT",FACE,{"disambiguationData":[TD([[makeQuery(id+"F0.imprint","IMPRINT",EDGE,{"derivedFrom":sQuery(id+"F0.wireOp",EDGE,"E27")}),1.0]])]});
            var Q1;
            {var subQ0=sQuery(id+"F0.wireOp",EDGE,"E30");Q1=makeQuery(id+"F0.imprint","IMPRINT",FACE,{"disambiguationData":[TD([[makeQuery(id+"F0.imprint","IMPRINT",EDGE,{"derivedFrom":subQ0}),-1.0]])]});}
            var Q2;
            {var subQ0=sQuery(id+"F0.wireOp",EDGE,"E34");Q2=makeQuery(id+"F0.imprint","IMPRINT",FACE,{"disambiguationData":[TD([[makeQuery(id+"F0.imprint","IMPRINT",EDGE,{"derivedFrom":subQ0}),1.0]])]});}
            var Q3;
            {var subQ0=sQuery(id+"F0.wireOp",EDGE,"E32");Q3=makeQuery(id+"F0.imprint","IMPRINT",FACE,{"disambiguationData":[TD([[makeQuery(id+"F0.imprint","IMPRINT",EDGE,{"derivedFrom":subQ0}),-1.0]])]});}
            var Q4;
            {var subQ0=sQuery(id+"F0.wireOp",EDGE,"E36");Q4=makeQuery(id+"F0.imprint","IMPRINT",FACE,{"disambiguationData":[TD([[makeQuery(id+"F0.imprint","IMPRINT",EDGE,{"derivedFrom":subQ0}),1.0]])]});}
            var Q5;
            {var subQ0=sQuery(id+"F0.wireOp",EDGE,"E38");Q5=makeQuery(id+"F0.imprint","IMPRINT",FACE,{"disambiguationData":[TD([[makeQuery(id+"F0.imprint","IMPRINT",EDGE,{"derivedFrom":subQ0}),1.0]])]});}
            var Q6;
            {var subQ0=sQuery(id+"F0.wireOp",EDGE,"E40");Q6=makeQuery(id+"F0.imprint","IMPRINT",FACE,{"disambiguationData":[TD([[makeQuery(id+"F0.imprint","IMPRINT",EDGE,{"derivedFrom":subQ0}),1.0]])]});}
            var Q7;
            {var subQ0=sQuery(id+"F0.wireOp",EDGE,"E46");Q7=makeQuery(id+"F0.imprint","IMPRINT",FACE,{"disambiguationData":[TD([[makeQuery(id+"F0.imprint","IMPRINT",EDGE,{"derivedFrom":subQ0}),-1.0]])]});}
            var Q8;
            {var subQ0=sQuery(id+"F0.wireOp",EDGE,"E48");Q8=makeQuery(id+"F0.imprint","IMPRINT",FACE,{"disambiguationData":[TD([[makeQuery(id+"F0.imprint","IMPRINT",EDGE,{"derivedFrom":subQ0}),-1.0]])]});}
            var Q9;
            {var subQ0=sQuery(id+"F0.wireOp",EDGE,"E44");Q9=makeQuery(id+"F0.imprint","IMPRINT",FACE,{"disambiguationData":[TD([[makeQuery(id+"F0.imprint","IMPRINT",EDGE,{"derivedFrom":subQ0}),-1.0]])]});}
            var Q10;
            {var subQ0=sQuery(id+"F0.wireOp",EDGE,"E42");Q10=makeQuery(id+"F0.imprint","IMPRINT",FACE,{"disambiguationData":[TD([[makeQuery(id+"F0.imprint","IMPRINT",EDGE,{"derivedFrom":subQ0}),-1.0]])]});}
            var Q11;
            Q11=makeQuery(id+"F0.imprint","IMPRINT",FACE,{"disambiguationData":[TD([[makeQuery(id+"F0.imprint","IMPRINT",EDGE,{"derivedFrom":sQuery(id+"F0.wireOp",EDGE,"E50")}),1.0]])]});
            var Q12;
            {var subQ0=sQuery(id+"F0.wireOp",EDGE,"E59");Q12=makeQuery(id+"F0.imprint","IMPRINT",FACE,{"disambiguationData":[TD([[makeQuery(id+"F0.imprint","IMPRINT",EDGE,{"derivedFrom":subQ0}),-1.0]])]});}
            var Q13;
            {var subQ0=sQuery(id+"F0.wireOp",EDGE,"E53");Q13=makeQuery(id+"F0.imprint","IMPRINT",FACE,{"disambiguationData":[TD([[makeQuery(id+"F0.imprint","IMPRINT",EDGE,{"derivedFrom":subQ0}),-1.0]])]});}
            var Q14;
            {var subQ0=sQuery(id+"F0.wireOp",EDGE,"E55");Q14=makeQuery(id+"F0.imprint","IMPRINT",FACE,{"disambiguationData":[TD([[makeQuery(id+"F0.imprint","IMPRINT",EDGE,{"derivedFrom":subQ0}),-1.0]])]});}
            var Q15;
            {var subQ0=sQuery(id+"F0.wireOp",EDGE,"E57");Q15=makeQuery(id+"F0.imprint","IMPRINT",FACE,{"disambiguationData":[TD([[makeQuery(id+"F0.imprint","IMPRINT",EDGE,{"derivedFrom":subQ0}),-1.0]])]});}
            var Q16;
            {var subQ0=sQuery(id+"F0.wireOp",EDGE,"E69");Q16=makeQuery(id+"F0.imprint","IMPRINT",FACE,{"disambiguationData":[TD([[makeQuery(id+"F0.imprint","IMPRINT",EDGE,{"derivedFrom":subQ0}),1.0]])]});}
            var Q17;
            {var subQ0=sQuery(id+"F0.wireOp",EDGE,"E71");Q17=makeQuery(id+"F0.imprint","IMPRINT",FACE,{"disambiguationData":[TD([[makeQuery(id+"F0.imprint","IMPRINT",EDGE,{"derivedFrom":subQ0}),-1.0]])]});}
            var Q18;
            {var subQ0=sQuery(id+"F0.wireOp",EDGE,"E67");Q18=makeQuery(id+"F0.imprint","IMPRINT",FACE,{"disambiguationData":[TD([[makeQuery(id+"F0.imprint","IMPRINT",EDGE,{"derivedFrom":subQ0}),1.0]])]});}
            var Q19;
            {var subQ0=sQuery(id+"F0.wireOp",EDGE,"E65");Q19=makeQuery(id+"F0.imprint","IMPRINT",FACE,{"disambiguationData":[TD([[makeQuery(id+"F0.imprint","IMPRINT",EDGE,{"derivedFrom":subQ0}),-1.0]])]});}
            var Q20;
            {var subQ0=sQuery(id+"F0.wireOp",EDGE,"E61");Q20=makeQuery(id+"F0.imprint","IMPRINT",FACE,{"disambiguationData":[TD([[makeQuery(id+"F0.imprint","IMPRINT",EDGE,{"derivedFrom":subQ0}),-1.0]])]});}
            var Q21;
            {var subQ0=sQuery(id+"F0.wireOp",EDGE,"E63");Q21=makeQuery(id+"F0.imprint","IMPRINT",FACE,{"disambiguationData":[TD([[makeQuery(id+"F0.imprint","IMPRINT",EDGE,{"derivedFrom":subQ0}),1.0]])]});}
            var Q22;
            {var subQ0=sQuery(id+"F0.wireOp",EDGE,"E29");var subQ4=makeQuery(id+"F0.imprint","INTERSECT",VERTEX,{"derivedFrom":[subQ0,sQuery(id+"F0.wireOp",EDGE,"E36"),sQuery(id+"F0.wireOp",EDGE,"E37")]});Q22=makeQuery(id+"F0.imprint","IMPRINT",FACE,{"disambiguationData":[TD([[makeQuery(id+"F0.imprint","IMPRINT",EDGE,{"disambiguationData":[TD([[subQ4,1.0]])],"derivedFrom":subQ0}),1.0]])]});}
            var Q23;
            {var subQ0=sQuery(id+"F0.wireOp",EDGE,"E52");var subQ4=makeQuery(id+"F0.imprint","INTERSECT",VERTEX,{"derivedFrom":[subQ0,sQuery(id+"F0.wireOp",EDGE,"E59"),sQuery(id+"F0.wireOp",EDGE,"E60")]});Q23=makeQuery(id+"F0.imprint","IMPRINT",FACE,{"disambiguationData":[TD([[makeQuery(id+"F0.imprint","IMPRINT",EDGE,{"disambiguationData":[TD([[subQ4,1.0]])],"derivedFrom":subQ0}),1.0]])]});}
            extrude(context, id + "F17", {"entities" : qUnion([Q0, Q1, Q2, Q3, Q4, Q5, Q6, Q7, Q8, Q9, Q10, Q11, Q12, Q13, Q14, Q15, Q16, Q17, Q18, Q19, Q20, Q21, Q22, Q23]), "depth" : 20.04 * mm, "hasSecondDirection" : true, "secondDirectionOppositeDirection" : false, "secondDirectionDepth" : 10.92 * mm});
        }
        {
            var Q0;
            Q0=makeQuery(id+"F0.imprint","IMPRINT",FACE,{"disambiguationData":[TD([[makeQuery(id+"F0.imprint","IMPRINT",EDGE,{"derivedFrom":sQuery(id+"F0.wireOp",EDGE,"E2")}),1.0]])]});
            var Q1;
            {var subQ0=sQuery(id+"F0.wireOp",EDGE,"E53");Q1=makeQuery(id+"F0.imprint","IMPRINT",FACE,{"disambiguationData":[TD([[makeQuery(id+"F0.imprint","IMPRINT",EDGE,{"derivedFrom":subQ0}),1.0]])]});}
            var Q2;
            {var subQ0=sQuery(id+"F0.wireOp",EDGE,"E54");Q2=makeQuery(id+"F0.imprint","IMPRINT",FACE,{"disambiguationData":[TD([[makeQuery(id+"F0.imprint","IMPRINT",EDGE,{"derivedFrom":subQ0}),-1.0]])]});}
            var Q3;
            {var subQ0=sQuery(id+"F0.wireOp",EDGE,"E60");Q3=makeQuery(id+"F0.imprint","IMPRINT",FACE,{"disambiguationData":[TD([[makeQuery(id+"F0.imprint","IMPRINT",EDGE,{"derivedFrom":subQ0}),-1.0]])]});}
            var Q4;
            {var subQ0=sQuery(id+"F0.wireOp",EDGE,"E66");Q4=makeQuery(id+"F0.imprint","IMPRINT",FACE,{"disambiguationData":[TD([[makeQuery(id+"F0.imprint","IMPRINT",EDGE,{"derivedFrom":subQ0}),-1.0]])]});}
            var Q5;
            {var subQ0=sQuery(id+"F0.wireOp",EDGE,"E62");Q5=makeQuery(id+"F0.imprint","IMPRINT",FACE,{"disambiguationData":[TD([[makeQuery(id+"F0.imprint","IMPRINT",EDGE,{"derivedFrom":subQ0}),1.0]])]});}
            var Q6;
            {var subQ0=sQuery(id+"F0.wireOp",EDGE,"E64");Q6=makeQuery(id+"F0.imprint","IMPRINT",FACE,{"disambiguationData":[TD([[makeQuery(id+"F0.imprint","IMPRINT",EDGE,{"derivedFrom":subQ0}),-1.0]])]});}
            var Q7;
            {var subQ0=sQuery(id+"F0.wireOp",EDGE,"E58");Q7=makeQuery(id+"F0.imprint","IMPRINT",FACE,{"disambiguationData":[TD([[makeQuery(id+"F0.imprint","IMPRINT",EDGE,{"derivedFrom":subQ0}),1.0]])]});}
            var Q8;
            {var subQ0=sQuery(id+"F0.wireOp",EDGE,"E56");Q8=makeQuery(id+"F0.imprint","IMPRINT",FACE,{"disambiguationData":[TD([[makeQuery(id+"F0.imprint","IMPRINT",EDGE,{"derivedFrom":subQ0}),1.0]])]});}
            var Q9;
            {var subQ0=sQuery(id+"F0.wireOp",EDGE,"E70");Q9=makeQuery(id+"F0.imprint","IMPRINT",FACE,{"disambiguationData":[TD([[makeQuery(id+"F0.imprint","IMPRINT",EDGE,{"derivedFrom":subQ0}),1.0]])]});}
            var Q10;
            {var subQ0=sQuery(id+"F0.wireOp",EDGE,"E61");Q10=makeQuery(id+"F0.imprint","IMPRINT",FACE,{"disambiguationData":[TD([[makeQuery(id+"F0.imprint","IMPRINT",EDGE,{"derivedFrom":subQ0}),1.0]])]});}
            var Q11;
            Q11=makeQuery(id+"F0.imprint","IMPRINT",FACE,{"disambiguationData":[TD([[makeQuery(id+"F0.imprint","IMPRINT",EDGE,{"derivedFrom":sQuery(id+"F0.wireOp",EDGE,"E0")}),1.0]])]});
            var Q12;
            {var subQ0=sQuery(id+"F0.wireOp",EDGE,"E30");Q12=makeQuery(id+"F0.imprint","IMPRINT",FACE,{"disambiguationData":[TD([[makeQuery(id+"F0.imprint","IMPRINT",EDGE,{"derivedFrom":subQ0}),1.0]])]});}
            var Q13;
            {var subQ0=sQuery(id+"F0.wireOp",EDGE,"E33");Q13=makeQuery(id+"F0.imprint","IMPRINT",FACE,{"disambiguationData":[TD([[makeQuery(id+"F0.imprint","IMPRINT",EDGE,{"derivedFrom":subQ0}),-1.0]])]});}
            var Q14;
            {var subQ0=sQuery(id+"F0.wireOp",EDGE,"E37");Q14=makeQuery(id+"F0.imprint","IMPRINT",FACE,{"disambiguationData":[TD([[makeQuery(id+"F0.imprint","IMPRINT",EDGE,{"derivedFrom":subQ0}),-1.0]])]});}
            var Q15;
            {var subQ0=sQuery(id+"F0.wireOp",EDGE,"E43");Q15=makeQuery(id+"F0.imprint","IMPRINT",FACE,{"disambiguationData":[TD([[makeQuery(id+"F0.imprint","IMPRINT",EDGE,{"derivedFrom":subQ0}),-1.0]])]});}
            var Q16;
            {var subQ0=sQuery(id+"F0.wireOp",EDGE,"E45");Q16=makeQuery(id+"F0.imprint","IMPRINT",FACE,{"disambiguationData":[TD([[makeQuery(id+"F0.imprint","IMPRINT",EDGE,{"derivedFrom":subQ0}),-1.0]])]});}
            var Q17;
            {var subQ0=sQuery(id+"F0.wireOp",EDGE,"E41");Q17=makeQuery(id+"F0.imprint","IMPRINT",FACE,{"disambiguationData":[TD([[makeQuery(id+"F0.imprint","IMPRINT",EDGE,{"derivedFrom":subQ0}),1.0]])]});}
            var Q18;
            {var subQ0=sQuery(id+"F0.wireOp",EDGE,"E35");Q18=makeQuery(id+"F0.imprint","IMPRINT",FACE,{"disambiguationData":[TD([[makeQuery(id+"F0.imprint","IMPRINT",EDGE,{"derivedFrom":subQ0}),1.0]])]});}
            var Q19;
            {var subQ0=sQuery(id+"F0.wireOp",EDGE,"E31");Q19=makeQuery(id+"F0.imprint","IMPRINT",FACE,{"disambiguationData":[TD([[makeQuery(id+"F0.imprint","IMPRINT",EDGE,{"derivedFrom":subQ0}),1.0]])]});}
            var Q20;
            {var subQ0=sQuery(id+"F0.wireOp",EDGE,"E39");Q20=makeQuery(id+"F0.imprint","IMPRINT",FACE,{"disambiguationData":[TD([[makeQuery(id+"F0.imprint","IMPRINT",EDGE,{"derivedFrom":subQ0}),1.0]])]});}
            var Q21;
            {var subQ0=sQuery(id+"F0.wireOp",EDGE,"E47");Q21=makeQuery(id+"F0.imprint","IMPRINT",FACE,{"disambiguationData":[TD([[makeQuery(id+"F0.imprint","IMPRINT",EDGE,{"derivedFrom":subQ0}),1.0]])]});}
            extrude(context, id + "F18", {"entities" : qUnion([Q0, Q1, Q2, Q3, Q4, Q5, Q6, Q7, Q8, Q9, Q10, Q11, Q12, Q13, Q14, Q15, Q16, Q17, Q18, Q19, Q20, Q21]), "oppositeDirection" : true, "depth" : 20.07 * mm, "hasSecondDirection" : true, "secondDirectionOppositeDirection" : true, "secondDirectionDepth" : 10.92 * mm});
        }
        {
            var Q0;
            {var subQ0=sQuery(id+"F0.wireOp",EDGE,"E32");Q0=makeQuery(id+"F0.imprint","IMPRINT",FACE,{"disambiguationData":[TD([[makeQuery(id+"F0.imprint","IMPRINT",EDGE,{"derivedFrom":subQ0}),-1.0]])]});}
            var Q1;
            {var subQ0=sQuery(id+"F0.wireOp",EDGE,"E30");Q1=makeQuery(id+"F0.imprint","IMPRINT",FACE,{"disambiguationData":[TD([[makeQuery(id+"F0.imprint","IMPRINT",EDGE,{"derivedFrom":subQ0}),-1.0]])]});}
            var Q2;
            {var subQ0=sQuery(id+"F0.wireOp",EDGE,"E34");Q2=makeQuery(id+"F0.imprint","IMPRINT",FACE,{"disambiguationData":[TD([[makeQuery(id+"F0.imprint","IMPRINT",EDGE,{"derivedFrom":subQ0}),1.0]])]});}
            var Q3;
            {var subQ0=sQuery(id+"F0.wireOp",EDGE,"E38");Q3=makeQuery(id+"F0.imprint","IMPRINT",FACE,{"disambiguationData":[TD([[makeQuery(id+"F0.imprint","IMPRINT",EDGE,{"derivedFrom":subQ0}),1.0]])]});}
            var Q4;
            {var subQ0=sQuery(id+"F0.wireOp",EDGE,"E40");Q4=makeQuery(id+"F0.imprint","IMPRINT",FACE,{"disambiguationData":[TD([[makeQuery(id+"F0.imprint","IMPRINT",EDGE,{"derivedFrom":subQ0}),1.0]])]});}
            var Q5;
            {var subQ0=sQuery(id+"F0.wireOp",EDGE,"E46");Q5=makeQuery(id+"F0.imprint","IMPRINT",FACE,{"disambiguationData":[TD([[makeQuery(id+"F0.imprint","IMPRINT",EDGE,{"derivedFrom":subQ0}),-1.0]])]});}
            var Q6;
            {var subQ0=sQuery(id+"F0.wireOp",EDGE,"E48");Q6=makeQuery(id+"F0.imprint","IMPRINT",FACE,{"disambiguationData":[TD([[makeQuery(id+"F0.imprint","IMPRINT",EDGE,{"derivedFrom":subQ0}),-1.0]])]});}
            var Q7;
            {var subQ0=sQuery(id+"F0.wireOp",EDGE,"E44");Q7=makeQuery(id+"F0.imprint","IMPRINT",FACE,{"disambiguationData":[TD([[makeQuery(id+"F0.imprint","IMPRINT",EDGE,{"derivedFrom":subQ0}),-1.0]])]});}
            var Q8;
            {var subQ0=sQuery(id+"F0.wireOp",EDGE,"E42");Q8=makeQuery(id+"F0.imprint","IMPRINT",FACE,{"disambiguationData":[TD([[makeQuery(id+"F0.imprint","IMPRINT",EDGE,{"derivedFrom":subQ0}),-1.0]])]});}
            var Q9;
            {var subQ0=sQuery(id+"F0.wireOp",EDGE,"E36");Q9=makeQuery(id+"F0.imprint","IMPRINT",FACE,{"disambiguationData":[TD([[makeQuery(id+"F0.imprint","IMPRINT",EDGE,{"derivedFrom":subQ0}),1.0]])]});}
            var Q10;
            Q10=makeQuery(id+"F0.imprint","IMPRINT",FACE,{"disambiguationData":[TD([[makeQuery(id+"F0.imprint","IMPRINT",EDGE,{"derivedFrom":sQuery(id+"F0.wireOp",EDGE,"E27")}),1.0]])]});
            var Q11;
            {var subQ0=sQuery(id+"F0.wireOp",EDGE,"E53");Q11=makeQuery(id+"F0.imprint","IMPRINT",FACE,{"disambiguationData":[TD([[makeQuery(id+"F0.imprint","IMPRINT",EDGE,{"derivedFrom":subQ0}),-1.0]])]});}
            var Q12;
            {var subQ0=sQuery(id+"F0.wireOp",EDGE,"E59");Q12=makeQuery(id+"F0.imprint","IMPRINT",FACE,{"disambiguationData":[TD([[makeQuery(id+"F0.imprint","IMPRINT",EDGE,{"derivedFrom":subQ0}),-1.0]])]});}
            var Q13;
            {var subQ0=sQuery(id+"F0.wireOp",EDGE,"E65");Q13=makeQuery(id+"F0.imprint","IMPRINT",FACE,{"disambiguationData":[TD([[makeQuery(id+"F0.imprint","IMPRINT",EDGE,{"derivedFrom":subQ0}),-1.0]])]});}
            var Q14;
            {var subQ0=sQuery(id+"F0.wireOp",EDGE,"E67");Q14=makeQuery(id+"F0.imprint","IMPRINT",FACE,{"disambiguationData":[TD([[makeQuery(id+"F0.imprint","IMPRINT",EDGE,{"derivedFrom":subQ0}),1.0]])]});}
            var Q15;
            {var subQ0=sQuery(id+"F0.wireOp",EDGE,"E61");Q15=makeQuery(id+"F0.imprint","IMPRINT",FACE,{"disambiguationData":[TD([[makeQuery(id+"F0.imprint","IMPRINT",EDGE,{"derivedFrom":subQ0}),-1.0]])]});}
            var Q16;
            {var subQ0=sQuery(id+"F0.wireOp",EDGE,"E63");Q16=makeQuery(id+"F0.imprint","IMPRINT",FACE,{"disambiguationData":[TD([[makeQuery(id+"F0.imprint","IMPRINT",EDGE,{"derivedFrom":subQ0}),1.0]])]});}
            var Q17;
            {var subQ0=sQuery(id+"F0.wireOp",EDGE,"E71");Q17=makeQuery(id+"F0.imprint","IMPRINT",FACE,{"disambiguationData":[TD([[makeQuery(id+"F0.imprint","IMPRINT",EDGE,{"derivedFrom":subQ0}),-1.0]])]});}
            var Q18;
            {var subQ0=sQuery(id+"F0.wireOp",EDGE,"E69");Q18=makeQuery(id+"F0.imprint","IMPRINT",FACE,{"disambiguationData":[TD([[makeQuery(id+"F0.imprint","IMPRINT",EDGE,{"derivedFrom":subQ0}),1.0]])]});}
            var Q19;
            {var subQ0=sQuery(id+"F0.wireOp",EDGE,"E57");Q19=makeQuery(id+"F0.imprint","IMPRINT",FACE,{"disambiguationData":[TD([[makeQuery(id+"F0.imprint","IMPRINT",EDGE,{"derivedFrom":subQ0}),-1.0]])]});}
            var Q20;
            {var subQ0=sQuery(id+"F0.wireOp",EDGE,"E55");Q20=makeQuery(id+"F0.imprint","IMPRINT",FACE,{"disambiguationData":[TD([[makeQuery(id+"F0.imprint","IMPRINT",EDGE,{"derivedFrom":subQ0}),-1.0]])]});}
            var Q21;
            Q21=makeQuery(id+"F0.imprint","IMPRINT",FACE,{"disambiguationData":[TD([[makeQuery(id+"F0.imprint","IMPRINT",EDGE,{"derivedFrom":sQuery(id+"F0.wireOp",EDGE,"E50")}),1.0]])]});
            var Q22;
            {var subQ0=sQuery(id+"F0.wireOp",EDGE,"E52");var subQ4=makeQuery(id+"F0.imprint","INTERSECT",VERTEX,{"derivedFrom":[subQ0,sQuery(id+"F0.wireOp",EDGE,"E59"),sQuery(id+"F0.wireOp",EDGE,"E60")]});Q22=makeQuery(id+"F0.imprint","IMPRINT",FACE,{"disambiguationData":[TD([[makeQuery(id+"F0.imprint","IMPRINT",EDGE,{"disambiguationData":[TD([[subQ4,1.0]])],"derivedFrom":subQ0}),1.0]])]});}
            var Q23;
            {var subQ0=sQuery(id+"F0.wireOp",EDGE,"E29");var subQ4=makeQuery(id+"F0.imprint","INTERSECT",VERTEX,{"derivedFrom":[subQ0,sQuery(id+"F0.wireOp",EDGE,"E36"),sQuery(id+"F0.wireOp",EDGE,"E37")]});Q23=makeQuery(id+"F0.imprint","IMPRINT",FACE,{"disambiguationData":[TD([[makeQuery(id+"F0.imprint","IMPRINT",EDGE,{"disambiguationData":[TD([[subQ4,1.0]])],"derivedFrom":subQ0}),1.0]])]});}
            extrude(context, id + "F19", {"entities" : qUnion([Q0, Q1, Q2, Q3, Q4, Q5, Q6, Q7, Q8, Q9, Q10, Q11, Q12, Q13, Q14, Q15, Q16, Q17, Q18, Q19, Q20, Q21, Q22, Q23]), "oppositeDirection" : true, "depth" : 19.99 * mm, "hasSecondDirection" : true, "secondDirectionOppositeDirection" : true, "secondDirectionDepth" : 10.97 * mm});
        }
        {
            var Q0;
            Q0=sQuery(id+"F0.wireOp",EDGE,"E17");
            extrude(context, id + "F20", {"bodyType" : ToolBodyType.SURFACE, "surfaceEntities" : qUnion([Q0]), "depth" : 20.26 * mm, "hasSecondDirection" : true, "secondDirectionOppositeDirection" : true, "secondDirectionDepth" : 20.27 * mm});
        }
        {
            var Q0;
            Q0=qCreatedBy(makeId("Front.planeOp"),FACE);
            var sketch = newSketch(context, id + "F21", { "sketchPlane" : qUnion([Q0])});
            skFitSpline(sketch, "E128", {"points": [v(8, 10.97) * mm, v(9.75, 12.72) * mm, v(12.87, 14.03) * mm, v(15.41, 14.82) * mm, v(17.44, 14.98) * mm, v(18.26, 12.98) * mm, v(17.42, 11.58) * mm, v(16.24, 11.05) * mm, v(14.32, 10.67) * mm, v(12.07, 10.45) * mm, v(8.66, 10.45) * mm, v(8, 10.97) * mm]});
            skFitSpline(sketch, "E129", {"points": [v(-8.51, 10.97) * mm, v(-10.03, 12.72) * mm, v(-12.87, 14.03) * mm, v(-15.8, 14.82) * mm, v(-17.63, 14.98) * mm, v(-18.22, 12.98) * mm, v(-17.42, 11.58) * mm, v(-15.93, 11.05) * mm, v(-14.06, 10.67) * mm, v(-11.71, 10.45) * mm, v(-9.16, 10.45) * mm, v(-8.51, 10.97) * mm]});
            skLineSegment(sketch, "E130.bottom", {"start": v(4.14, 13.21) * mm, "end": v(-4.33, 13.21) * mm});
            skLineSegment(sketch, "E130.top", {"start": v(4.14, 9.3) * mm, "end": v(-4.33, 9.3) * mm});
            skLineSegment(sketch, "E130.left", {"start": v(5.4, 11.94) * mm, "end": v(5.4, 10.56) * mm});
            skLineSegment(sketch, "E130.right", {"start": v(-5.6, 11.94) * mm, "end": v(-5.6, 10.56) * mm});
            skPoint(sketch, "E131.visualSharp", {"position": v(5.4, 13.21) * mm});
            skArc(sketch, "E131.filletArc", {"start": v(5.4, 11.94) * mm, "mid": v(5.03, 12.84) * mm, "end": v(4.14, 13.21) * mm});
            skPoint(sketch, "E132.visualSharp", {"position": v(-5.6, 13.21) * mm});
            skArc(sketch, "E132.filletArc", {"start": v(-4.33, 13.21) * mm, "mid": v(-5.23, 12.84) * mm, "end": v(-5.6, 11.94) * mm});
            skPoint(sketch, "E133.visualSharp", {"position": v(-5.6, 9.3) * mm});
            skArc(sketch, "E133.filletArc", {"start": v(-5.6, 10.56) * mm, "mid": v(-5.23, 9.66) * mm, "end": v(-4.33, 9.3) * mm});
            skPoint(sketch, "E134.visualSharp", {"position": v(5.4, 9.3) * mm});
            skArc(sketch, "E134.filletArc", {"start": v(4.14, 9.3) * mm, "mid": v(5.03, 9.66) * mm, "end": v(5.4, 10.56) * mm});
            skSolve(sketch);
        }
        {
            var Q0;
            Q0=sQuery(id+"F0.wireOp",EDGE,"E74");
            extrude(context, id + "F22", {"bodyType" : ToolBodyType.SURFACE, "surfaceEntities" : qUnion([Q0]), "depth" : 17.02 * mm, "hasSecondDirection" : true, "secondDirectionOppositeDirection" : true, "secondDirectionDepth" : 17.02 * mm});
        }
        {
            var Q0;
            Q0=makeQuery(id+"F21.imprint","IMPRINT",FACE,{"disambiguationData":[TD([[makeQuery(id+"F21.imprint","IMPRINT",EDGE,{"derivedFrom":sQuery(id+"F21.wireOp",EDGE,"E129")}),1.0]])]});
            var Q1;
            Q1=makeQuery(id+"F21.imprint","IMPRINT",FACE,{"disambiguationData":[TD([[makeQuery(id+"F21.imprint","IMPRINT",EDGE,{"derivedFrom":sQuery(id+"F21.wireOp",EDGE,"E128")}),-1.0]])]});
            extrude(context, id + "F23", {"entities" : qUnion([Q0, Q1]), "oppositeDirection" : true, "depth" : 77.22 * mm, "hasSecondDirection" : true, "secondDirectionOppositeDirection" : true, "secondDirectionDepth" : 71.12 * mm});
        }
        {
            var Q0;
            Q0=makeQuery(id+"F21.imprint","IMPRINT",FACE,{"disambiguationData":[TD([[makeQuery(id+"F21.imprint","IMPRINT",EDGE,{"derivedFrom":sQuery(id+"F21.wireOp",EDGE,"E130.bottom")}),1.0]])]});
            extrude(context, id + "F24", {"entities" : qUnion([Q0]), "oppositeDirection" : true, "depth" : 77.62 * mm});
        }
        {
            var Q0;
            Q0=makeQuery(id+"F24.opExtrude","CAP_EDGE",EDGE,{"disambiguationData":[OSD([sQuery(id+"F21.wireOp",EDGE,"E130.bottom")])],"isStart":false});
            fillet(context, id + "F25", {"entities" : qUnion([Q0]), "radius" : 0.43 * mm, "tangentPropagation" : true, "allowEdgeOverflow" : false});
        }
        {
            var Q0;
            Q0=makeQuery(id+"F6.imprint","IMPRINT",FACE,{"disambiguationData":[TD([[makeQuery(id+"F6.imprint","IMPRINT",EDGE,{"derivedFrom":sQuery(id+"F6.wireOp",EDGE,"E98")}),1.0]])]});
            var Q1;
            Q1=makeQuery(id+"F6.imprint","IMPRINT",FACE,{"disambiguationData":[TD([[makeQuery(id+"F6.imprint","IMPRINT",EDGE,{"derivedFrom":sQuery(id+"F6.wireOp",EDGE,"E94")}),-1.0]])]});
            var Q2;
            Q2=makeQuery(id+"F6.imprint","IMPRINT",FACE,{"disambiguationData":[TD([[makeQuery(id+"F6.imprint","IMPRINT",EDGE,{"derivedFrom":sQuery(id+"F6.wireOp",EDGE,"E101")}),-1.0]])]});
            extrude(context, id + "F26", {"entities" : qUnion([Q0, Q1, Q2]), "depth" : 17.12 * mm, "hasSecondDirection" : true, "secondDirectionOppositeDirection" : false, "secondDirectionDepth" : 11.9 * mm});
        }
        {
            var Q0;
            {var subQ0=sQuery(id+"F6.wireOp",EDGE,"E110");Q0=makeQuery(id+"F6.imprint","IMPRINT",FACE,{"disambiguationData":[TD([[makeQuery(id+"F6.imprint","IMPRINT",EDGE,{"derivedFrom":subQ0}),1.0]])]});}
            var Q1;
            {var subQ0=sQuery(id+"F6.wireOp",EDGE,"E104");Q1=makeQuery(id+"F6.imprint","IMPRINT",FACE,{"disambiguationData":[TD([[makeQuery(id+"F6.imprint","IMPRINT",EDGE,{"derivedFrom":subQ0}),-1.0]])]});}
            var Q2;
            {var subQ0=sQuery(id+"F6.wireOp",EDGE,"E107");Q2=makeQuery(id+"F6.imprint","IMPRINT",FACE,{"disambiguationData":[TD([[makeQuery(id+"F6.imprint","IMPRINT",EDGE,{"derivedFrom":subQ0}),1.0]])]});}
            var Q3;
            {var subQ0=sQuery(id+"F6.wireOp",EDGE,"E112");Q3=makeQuery(id+"F6.imprint","IMPRINT",FACE,{"disambiguationData":[TD([[makeQuery(id+"F6.imprint","IMPRINT",EDGE,{"derivedFrom":subQ0}),1.0]])]});}
            var Q4;
            {var subQ0=sQuery(id+"F6.wireOp",EDGE,"E114");Q4=makeQuery(id+"F6.imprint","IMPRINT",FACE,{"disambiguationData":[TD([[makeQuery(id+"F6.imprint","IMPRINT",EDGE,{"derivedFrom":subQ0}),-1.0]])]});}
            var Q5;
            {var subQ0=sQuery(id+"F6.wireOp",EDGE,"E116");Q5=makeQuery(id+"F6.imprint","IMPRINT",FACE,{"disambiguationData":[TD([[makeQuery(id+"F6.imprint","IMPRINT",EDGE,{"derivedFrom":subQ0}),-1.0]])]});}
            extrude(context, id + "F27", {"entities" : qUnion([Q0, Q1, Q2, Q3, Q4, Q5]), "depth" : 16.65 * mm, "hasSecondDirection" : true, "secondDirectionOppositeDirection" : false, "secondDirectionDepth" : 15.24 * mm});
        }
        {
            var Q0;
            {var subQ0=sQuery(id+"F6.wireOp",EDGE,"E102");Q0=makeQuery(id+"F6.imprint","IMPRINT",FACE,{"disambiguationData":[TD([[makeQuery(id+"F6.imprint","IMPRINT",EDGE,{"derivedFrom":subQ0}),1.0]])]});}
            var Q1;
            {var subQ0=sQuery(id+"F6.wireOp",EDGE,"E94");Q1=makeQuery(id+"F6.imprint","IMPRINT",FACE,{"disambiguationData":[TD([[makeQuery(id+"F6.imprint","IMPRINT",EDGE,{"derivedFrom":subQ0}),-1.0]])]});}
            var Q2;
            {var subQ0=sQuery(id+"F6.wireOp",EDGE,"E106");Q2=makeQuery(id+"F6.imprint","IMPRINT",FACE,{"disambiguationData":[TD([[makeQuery(id+"F6.imprint","IMPRINT",EDGE,{"derivedFrom":subQ0}),1.0]])]});}
            var Q3;
            {var subQ0=sQuery(id+"F6.wireOp",EDGE,"E96");Q3=makeQuery(id+"F6.imprint","IMPRINT",FACE,{"disambiguationData":[TD([[makeQuery(id+"F6.imprint","IMPRINT",EDGE,{"derivedFrom":subQ0}),-1.0]])]});}
            var Q4;
            {var subQ0=sQuery(id+"F6.wireOp",EDGE,"E111");Q4=makeQuery(id+"F6.imprint","IMPRINT",FACE,{"disambiguationData":[TD([[makeQuery(id+"F6.imprint","IMPRINT",EDGE,{"derivedFrom":subQ0}),1.0]])]});}
            var Q5;
            {var subQ3=sQuery(id+"F6.wireOp",EDGE,"E113");Q5=makeQuery(id+"F6.imprint","IMPRINT",FACE,{"disambiguationData":[TD([[makeQuery(id+"F6.imprint","IMPRINT",EDGE,{"derivedFrom":subQ3}),1.0]])]});}
            var Q6;
            {var subQ3=sQuery(id+"F6.wireOp",EDGE,"E117");Q6=makeQuery(id+"F6.imprint","IMPRINT",FACE,{"disambiguationData":[TD([[makeQuery(id+"F6.imprint","IMPRINT",EDGE,{"derivedFrom":subQ3}),-1.0]])]});}
            var Q7;
            {var subQ0=sQuery(id+"F6.wireOp",EDGE,"E115");Q7=makeQuery(id+"F6.imprint","IMPRINT",FACE,{"disambiguationData":[TD([[makeQuery(id+"F6.imprint","IMPRINT",EDGE,{"derivedFrom":subQ0}),-1.0]])]});}
            var Q8;
            {var subQ0=sQuery(id+"F6.wireOp",EDGE,"E99");Q8=makeQuery(id+"F6.imprint","IMPRINT",FACE,{"disambiguationData":[TD([[makeQuery(id+"F6.imprint","IMPRINT",EDGE,{"derivedFrom":subQ0}),-1.0]])]});}
            extrude(context, id + "F28", {"entities" : qUnion([Q0, Q1, Q2, Q3, Q4, Q5, Q6, Q7, Q8]), "depth" : 17.12 * mm, "hasSecondDirection" : true, "secondDirectionOppositeDirection" : false, "secondDirectionDepth" : 9.68 * mm});
        }
        {
            var Q0;
            {var subQ5=sQuery(id+"F6.wireOp",EDGE,"E118");Q0=makeQuery(id+"F6.imprint","IMPRINT",FACE,{"disambiguationData":[TD([[makeQuery(id+"F6.imprint","IMPRINT",EDGE,{"derivedFrom":subQ5}),-1.0]])]});}
            var Q1;
            {var subQ5=sQuery(id+"F6.wireOp",EDGE,"E120");Q1=makeQuery(id+"F6.imprint","IMPRINT",FACE,{"disambiguationData":[TD([[makeQuery(id+"F6.imprint","IMPRINT",EDGE,{"derivedFrom":subQ5}),-1.0]])]});}
            extrude(context, id + "F29", {"entities" : qUnion([Q0, Q1]), "depth" : 17.2 * mm, "hasSecondDirection" : true, "secondDirectionOppositeDirection" : false, "secondDirectionDepth" : 9.14 * mm});
        }
        {
            var Q0;
            Q0=sQuery(id+"F0.wireOp",EDGE,"E75");
            extrude(context, id + "F30", {"bodyType" : ToolBodyType.SURFACE, "surfaceEntities" : qUnion([Q0]), "depth" : 17.27 * mm, "hasSecondDirection" : true, "secondDirectionOppositeDirection" : true, "secondDirectionDepth" : 17.27 * mm});
        }
        {
            var Q0;
            Q0=makeQuery(id+"F16.opExtrude","CAP_EDGE",EDGE,{"disambiguationData":[OSD([sQuery(id+"F0.wireOp",EDGE,"E2")])],"isStart":false});
            var Q1;
            Q1=makeQuery(id+"F16.opExtrude","CAP_EDGE",EDGE,{"disambiguationData":[OSD([sQuery(id+"F0.wireOp",EDGE,"E2")])],"isStart":true});
            var Q2;
            Q2=makeQuery(id+"F18.opExtrude","CAP_EDGE",EDGE,{"disambiguationData":[OSD([sQuery(id+"F0.wireOp",EDGE,"E2")])],"isStart":true});
            var Q3;
            Q3=makeQuery(id+"F18.opExtrude","CAP_EDGE",EDGE,{"disambiguationData":[OSD([sQuery(id+"F0.wireOp",EDGE,"E2")])],"isStart":false});
            var Q4;
            Q4=makeQuery(id+"F18.opExtrude","CAP_EDGE",EDGE,{"disambiguationData":[OSD([sQuery(id+"F0.wireOp",EDGE,"E0")])],"isStart":false});
            var Q5;
            Q5=makeQuery(id+"F18.opExtrude","CAP_EDGE",EDGE,{"disambiguationData":[OSD([sQuery(id+"F0.wireOp",EDGE,"E0")])],"isStart":true});
            var Q6;
            Q6=makeQuery(id+"F16.opExtrude","CAP_EDGE",EDGE,{"disambiguationData":[OSD([sQuery(id+"F0.wireOp",EDGE,"E0")])],"isStart":true});
            var Q7;
            Q7=makeQuery(id+"F16.opExtrude","CAP_EDGE",EDGE,{"disambiguationData":[OSD([sQuery(id+"F0.wireOp",EDGE,"E0")])],"isStart":false});
            fillet(context, id + "F31", {"entities" : qUnion([Q0, Q1, Q2, Q3, Q4, Q5, Q6, Q7]), "radius" : 1.27 * mm, "tangentPropagation" : true, "allowEdgeOverflow" : false});
        }
        {
            var Q0;
            Q0=makeQuery(id+"F4.opExtrude","CAP_FACE",FACE,{"disambiguationData":[OSD([sQuery(id+"F0.wireOp",EDGE,"E6"),sQuery(id+"F0.wireOp",EDGE,"E7"),sQuery(id+"F0.wireOp",EDGE,"E8"),sQuery(id+"F0.wireOp",EDGE,"E9"),sQuery(id+"F0.wireOp",EDGE,"E15"),sQuery(id+"F0.wireOp",EDGE,"E16"),sQuery(id+"F0.wireOp",EDGE,"E19"),sQuery(id+"F0.wireOp",EDGE,"E20"),sQuery(id+"F0.wireOp",EDGE,"E25"),sQuery(id+"F0.wireOp",EDGE,"E26")])],"isStart":false});
            var sketch = newSketch(context, id + "F32", { "sketchPlane" : qUnion([Q0])});
            skFitSpline(sketch, "E135", {"points": [v(13, 18.07) * mm, v(13.66, 18.36) * mm, v(14.87, 18.4) * mm, v(15.32, 18.14) * mm, v(15.3, 17.8) * mm, v(14.92, 17.52) * mm, v(14.07, 17.35) * mm, v(13.37, 17.47) * mm, v(13, 17.74) * mm, v(13, 18.07) * mm]});
            skSolve(sketch);
        }
        {
            var Q0;
            {var subQ0=sQuery(id+"F32.wireOp",EDGE,"E135");var subQ1=makeQuery(id+"F4.opExtrude","CAP_EDGE",EDGE,{"disambiguationData":[OSD([sQuery(id+"F0.wireOp",EDGE,"E6")])],"isStart":false});var subQ2=makeQuery(id+"F32.imprint","INTERSECT",VERTEX,{"disambiguationData":[OD(0.0)],"derivedFrom":[subQ1,subQ0]});Q0=makeQuery(id+"F32.imprint","IMPRINT",FACE,{"disambiguationData":[TD([[makeQuery(id+"F32.imprint","IMPRINT",EDGE,{"disambiguationData":[TD([[subQ2,1.0]])],"derivedFrom":subQ0}),-1.0]])]});}
            extrude(context, id + "F33", {"entities" : qUnion([Q0]), "depth" : 0.7 * mm, "hasSecondDirection" : true, "secondDirectionOppositeDirection" : true, "secondDirectionDepth" : 41.15 * mm});
        }
        {
            var Q0;
            Q0=qCreatedBy(makeId("Front.planeOp"),FACE);
            var sketch = newSketch(context, id + "F34", { "sketchPlane" : qUnion([Q0])});
            skFitSpline(sketch, "E136", {"points": [v(20.96, 18.43) * mm, v(21.22, 19.8) * mm, v(22.98, 20.2) * mm, v(24.68, 19.55) * mm, v(24.8, 17.7) * mm, v(24.13, 17.38) * mm, v(20.96, 17.36) * mm], "startDerivative": vector(0.47, 6.66) * mm, "endDerivative": vector(-13.75, 1.78) * mm});
            skFitSpline(sketch, "E137", {"points": [v(-20.9, 18.43) * mm, v(-21.08, 19.8) * mm, v(-23.1, 20.2) * mm, v(-24.9, 19.53) * mm, v(-25.01, 17.85) * mm, v(-24.11, 17.33) * mm, v(-20.9, 17.35) * mm], "startDerivative": vector(-1.02, 15.12) * mm, "endDerivative": vector(18.87, 0.81) * mm});
            skFitSpline(sketch, "E138", {"points": [v(-20.9, 18.43) * mm, v(-20.9, 17.35) * mm], "startDerivative": vector(0.02, -0.98) * mm, "endDerivative": vector(0.02, -0.98) * mm});
            skFitSpline(sketch, "E139", {"points": [v(20.96, 18.43) * mm, v(20.96, 17.36) * mm], "startDerivative": vector(-0.03, -0.8) * mm, "endDerivative": vector(0.04, -0.73) * mm});
            skSolve(sketch);
        }
        {
            var Q0;
            Q0=makeQuery(id+"F34.imprint","IMPRINT",FACE,{"disambiguationData":[TD([[makeQuery(id+"F34.imprint","IMPRINT",EDGE,{"derivedFrom":sQuery(id+"F34.wireOp",EDGE,"E136")}),-1.0]])]});
            var Q1;
            Q1=makeQuery(id+"F34.imprint","IMPRINT",FACE,{"disambiguationData":[TD([[makeQuery(id+"F34.imprint","IMPRINT",EDGE,{"derivedFrom":sQuery(id+"F34.wireOp",EDGE,"E137")}),1.0]])]});
            extrude(context, id + "F35", {"entities" : qUnion([Q0, Q1]), "operationType" : NewBodyOperationType.ADD, "oppositeDirection" : true, "depth" : 15.9 * mm, "hasSecondDirection" : true, "secondDirectionOppositeDirection" : true, "secondDirectionDepth" : 13.33 * mm});
        }
        {
            var Q0;
            Q0=makeQuery(id+"F35.opExtrude","CAP_FACE",FACE,{"disambiguationData":[OSD([sQuery(id+"F34.wireOp",EDGE,"E136"),sQuery(id+"F34.wireOp",EDGE,"E139")])],"isStart":true});
            var Q1;
            Q1=makeQuery(id+"F35.opExtrude","CAP_FACE",FACE,{"disambiguationData":[OSD([sQuery(id+"F34.wireOp",EDGE,"E137"),sQuery(id+"F34.wireOp",EDGE,"E138")])],"isStart":true});
            extrude(context, id + "F36", {"entities" : qUnion([Q0, Q1]), "operationType" : NewBodyOperationType.ADD, "depth" : 0.4 * mm});
        }
    });
